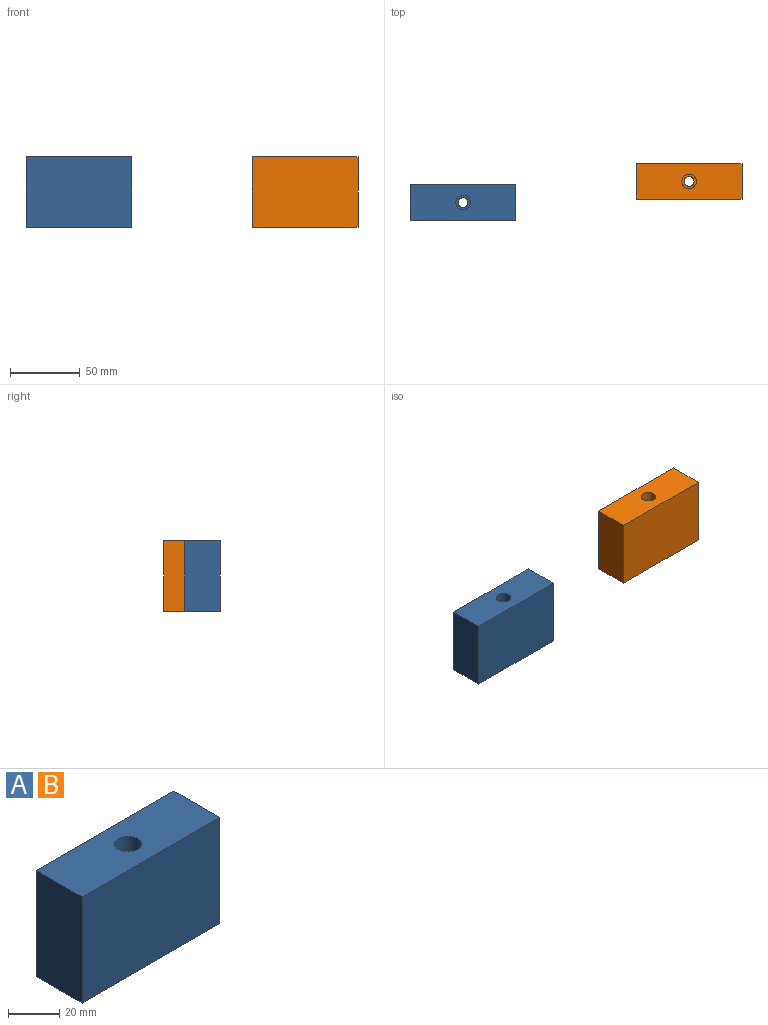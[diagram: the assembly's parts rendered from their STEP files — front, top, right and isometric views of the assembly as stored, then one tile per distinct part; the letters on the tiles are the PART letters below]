
ASSEMBLY  parts=2 mates=1
PART A: 9 faces, bbox 76.2x25.4x50.8 mm
  f0: plane 76.2x50.8mm, normal (0,-1,0), area 3871mm2, adj f1,f3,f4,f5
  f1: plane 50.8x25.4mm, normal (1,0,0), area 1290.3mm2, adj f0,f2,f4,f5
  f2: plane 76.2x50.8mm, normal (0,1,0), area 3871mm2, adj f1,f3,f4,f5
  f3: plane 50.8x25.4mm, normal (-1,0,0), area 1290.3mm2, adj f0,f2,f4,f5
  f4: plane 76.2x25.4mm, normal (0,0,1), area 1849.5mm2, adj f0,f1,f2,f3,f8
  f5: plane 76.2x25.4mm, normal (0,0,-1), area 1895.5mm2, adj f0,f1,f2,f3,f6
  f6: cylinder r=3.57mm len=43.94mm, axis (0,0,1), area 985.3mm2, adj f5,f7
  f7: plane 10.46x10.46mm, normal (0,0,1), area 46mm2, adj f6,f8
  f8: cylinder r=5.23mm len=10.46mm, axis (0,0,1), area 225.5mm2, adj f4,f7
PART B: same geometry as A
PLACE A at identity fixed
PLACE B t=(162.67,15.2,0)mm
MATE planar B.f6 <-> A.f6  axis (0,0,-1) through (162.67,15.2,0)mm
